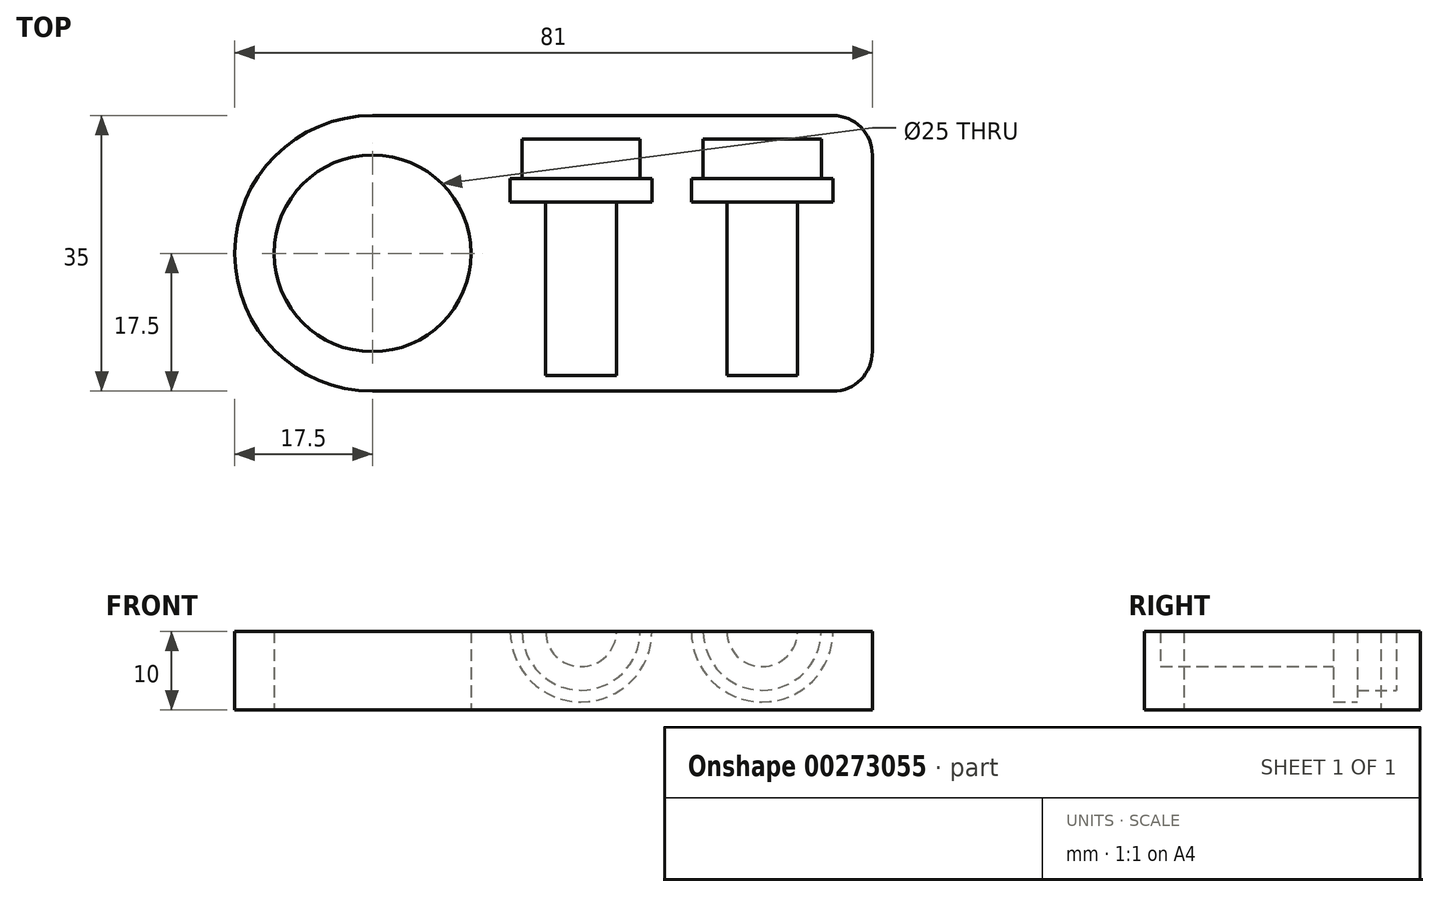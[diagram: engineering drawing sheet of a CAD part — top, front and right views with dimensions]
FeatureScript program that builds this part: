
annotation { "Feature Type Name" : "Feature", "Feature Type Description" : "" }
export const myFeature = defineFeature(function(context is Context, id is Id, definition is map)
    precondition{}
    {
        {
            var Q0;
            Q0=qCreatedBy(makeId("Top.planeOp"),FACE);
            var sketch = newSketch(context, id + "F0", { "sketchPlane" : qUnion([Q0])});
            skLineSegment(sketch, "E0.bottom", {"start": v(17.5, 0) * mm, "end": v(76, 0) * mm});
            skLineSegment(sketch, "E0.top", {"start": v(17.5, 35) * mm, "end": v(76, 35) * mm});
            skLineSegment(sketch, "E0.left", {"start": v(0, 17.5) * mm, "end": v(0, 17.5) * mm});
            skLineSegment(sketch, "E0.right", {"start": v(81, 5) * mm, "end": v(81, 30) * mm});
            skLineSegment(sketch, "E1.bottom", {"start": v(0, 0) * mm, "end": v(17.5, 0) * mm, "construction": true});
            skLineSegment(sketch, "E1.top", {"start": v(0, 17.5) * mm, "end": v(17.5, 17.5) * mm, "construction": true});
            skLineSegment(sketch, "E1.left", {"start": v(0, 0) * mm, "end": v(0, 17.5) * mm, "construction": true});
            skLineSegment(sketch, "E1.right", {"start": v(17.5, 0) * mm, "end": v(17.5, 17.5) * mm, "construction": true});
            skCircle(sketch, "E2", {"center": v(17.5, 17.5) * mm, "radius": 12.5 * mm});
            skPoint(sketch, "E3.visualSharp", {"position": v(0, 0) * mm});
            skArc(sketch, "E3.filletArc", {"start": v(0, 17.5) * mm, "mid": v(5.13, 5.13) * mm, "end": v(17.5, 0) * mm});
            skPoint(sketch, "E4.visualSharp", {"position": v(0, 35) * mm});
            skArc(sketch, "E4.filletArc", {"start": v(17.5, 35) * mm, "mid": v(5.13, 29.87) * mm, "end": v(0, 17.5) * mm});
            skPoint(sketch, "E5.visualSharp", {"position": v(81, 35) * mm});
            skArc(sketch, "E5.filletArc", {"start": v(81, 30) * mm, "mid": v(79.54, 33.54) * mm, "end": v(76, 35) * mm});
            skPoint(sketch, "E6.visualSharp", {"position": v(81, 0) * mm});
            skArc(sketch, "E6.filletArc", {"start": v(76, 0) * mm, "mid": v(79.54, 1.46) * mm, "end": v(81, 5) * mm});
            skSolve(sketch);
        }
        {
            var Q0;
            Q0=makeQuery(id+"F0.imprint","IMPRINT",FACE,{"disambiguationData":[TD([[makeQuery(id+"F0.imprint","IMPRINT",EDGE,{"derivedFrom":sQuery(id+"F0.wireOp",EDGE,"E0.bottom")}),1.0]])]});
            extrude(context, id + "F1", {"entities" : qUnion([Q0]), "depth" : 10 * mm});
        }
        {
            var Q0;
            Q0=makeQuery(id+"F1.opExtrude","CAP_FACE",FACE,{"disambiguationData":[OSD([sQuery(id+"F0.wireOp",EDGE,"E0.bottom"),sQuery(id+"F0.wireOp",EDGE,"E0.top"),sQuery(id+"F0.wireOp",EDGE,"E0.right"),sQuery(id+"F0.wireOp",EDGE,"E2"),sQuery(id+"F0.wireOp",EDGE,"E3.filletArc"),sQuery(id+"F0.wireOp",EDGE,"E4.filletArc"),sQuery(id+"F0.wireOp",EDGE,"E5.filletArc"),sQuery(id+"F0.wireOp",EDGE,"E6.filletArc")])],"isStart":false});
            var sketch = newSketch(context, id + "F2", { "sketchPlane" : qUnion([Q0])});
            skLineSegment(sketch, "E7.bottom", {"start": v(0, 0) * mm, "end": v(44, 0) * mm, "construction": true});
            skLineSegment(sketch, "E7.top", {"start": v(0, 2) * mm, "end": v(44, 2) * mm, "construction": true});
            skLineSegment(sketch, "E7.left", {"start": v(0, 0) * mm, "end": v(0, 2) * mm, "construction": true});
            skLineSegment(sketch, "E7.right", {"start": v(44, 0) * mm, "end": v(44, 2) * mm, "construction": true});
            skLineSegment(sketch, "E8.bottom", {"start": v(44, 2) * mm, "end": v(48.5, 2) * mm});
            skLineSegment(sketch, "E8.left", {"start": v(44, 2) * mm, "end": v(44, 24) * mm});
            skLineSegment(sketch, "E8.right", {"start": v(48.5, 2) * mm, "end": v(48.5, 24) * mm});
            skLineSegment(sketch, "E9.bottom", {"start": v(48.5, 24) * mm, "end": v(53, 24) * mm});
            skLineSegment(sketch, "E9.top", {"start": v(51.5, 27) * mm, "end": v(53, 27) * mm});
            skLineSegment(sketch, "E9.left", {"start": v(44, 24) * mm, "end": v(44, 27) * mm});
            skLineSegment(sketch, "E9.right", {"start": v(53, 24) * mm, "end": v(53, 27) * mm});
            skLineSegment(sketch, "E10.top", {"start": v(44, 32) * mm, "end": v(51.5, 32) * mm});
            skLineSegment(sketch, "E10.left", {"start": v(44, 27) * mm, "end": v(44, 32) * mm});
            skLineSegment(sketch, "E10.right", {"start": v(51.5, 27) * mm, "end": v(51.5, 32) * mm});
            skLineSegment(sketch, "E11", {"start": v(44, 2) * mm, "end": v(67, 2) * mm, "construction": true});
            skPoint(sketch, "E11.endSnap0", {"position": v(46.25, 2) * mm});
            skLineSegment(sketch, "E12.bottom", {"start": v(67, 2) * mm, "end": v(71.5, 2) * mm});
            skLineSegment(sketch, "E12.left", {"start": v(67, 2) * mm, "end": v(67, 24) * mm});
            skLineSegment(sketch, "E12.right", {"start": v(71.5, 2) * mm, "end": v(71.5, 24) * mm});
            skLineSegment(sketch, "E13.bottom", {"start": v(71.5, 24) * mm, "end": v(76, 24) * mm});
            skLineSegment(sketch, "E13.top", {"start": v(74.5, 27) * mm, "end": v(76, 27) * mm});
            skLineSegment(sketch, "E13.left", {"start": v(67, 24) * mm, "end": v(67, 27) * mm});
            skLineSegment(sketch, "E13.right", {"start": v(76, 24) * mm, "end": v(76, 27) * mm});
            skLineSegment(sketch, "E14.top", {"start": v(67, 32) * mm, "end": v(74.5, 32) * mm});
            skLineSegment(sketch, "E14.left", {"start": v(67, 27) * mm, "end": v(67, 32) * mm});
            skLineSegment(sketch, "E14.right", {"start": v(74.5, 27) * mm, "end": v(74.5, 32) * mm});
            skSolve(sketch);
        }
        {
            var Q0;
            Q0=makeQuery(id+"F2.imprint","IMPRINT",FACE,{"disambiguationData":[TD([[makeQuery(id+"F2.imprint","IMPRINT",EDGE,{"derivedFrom":sQuery(id+"F2.wireOp",EDGE,"E8.bottom")}),1.0]])]});
            var Q1;
            Q1=sQuery(id+"F2.wireOp",EDGE,"E8.left");
            revolve(context, id + "F3", {"operationType" : NewBodyOperationType.REMOVE, "entities" : qUnion([Q0]), "axis" : qUnion([Q1]), "revolveType" : RevolveType.FULL, "oppositeDirection" : true});
        }
        {
            var Q0;
            Q0=makeQuery(id+"F2.imprint","IMPRINT",FACE,{"disambiguationData":[TD([[makeQuery(id+"F2.imprint","IMPRINT",EDGE,{"derivedFrom":sQuery(id+"F2.wireOp",EDGE,"E12.bottom")}),1.0]])]});
            var Q1;
            Q1=sQuery(id+"F2.wireOp",EDGE,"E12.left");
            revolve(context, id + "F4", {"operationType" : NewBodyOperationType.REMOVE, "entities" : qUnion([Q0]), "axis" : qUnion([Q1]), "revolveType" : RevolveType.FULL, "oppositeDirection" : true});
        }
    });
